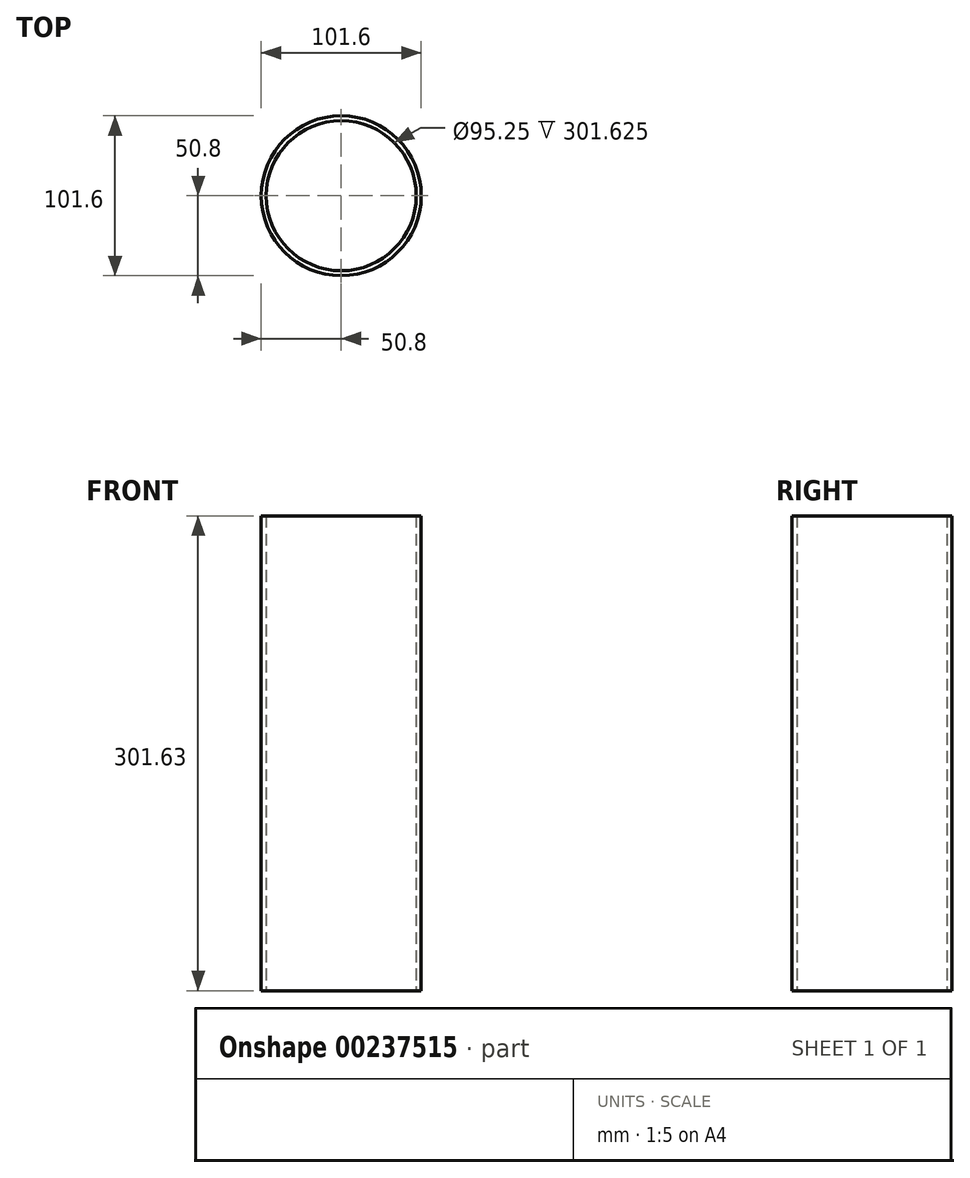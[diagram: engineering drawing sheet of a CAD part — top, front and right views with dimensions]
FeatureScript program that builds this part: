
annotation { "Feature Type Name" : "Feature", "Feature Type Description" : "" }
export const myFeature = defineFeature(function(context is Context, id is Id, definition is map)
    precondition{}
    {
        {
            var Q0;
            Q0=qCreatedBy(makeId("Top.planeOp"),FACE);
            var sketch = newSketch(context, id + "F0", { "sketchPlane" : qUnion([Q0])});
            skCircle(sketch, "E0", {"center": v(0, 0) * mm, "radius": 50.8 * mm});
            skCircle(sketch, "E1", {"center": v(0, 0) * mm, "radius": 47.63 * mm});
            skSolve(sketch);
        }
        {
            var Q0;
            Q0=makeQuery(id+"F0.imprint","IMPRINT",FACE,{"disambiguationData":[TD([[makeQuery(id+"F0.imprint","IMPRINT",EDGE,{"derivedFrom":sQuery(id+"F0.wireOp",EDGE,"E0")}),1.0]])]});
            extrude(context, id + "F1", {"entities" : qUnion([Q0]), "depth" : 301.62 * mm});
        }
    });
